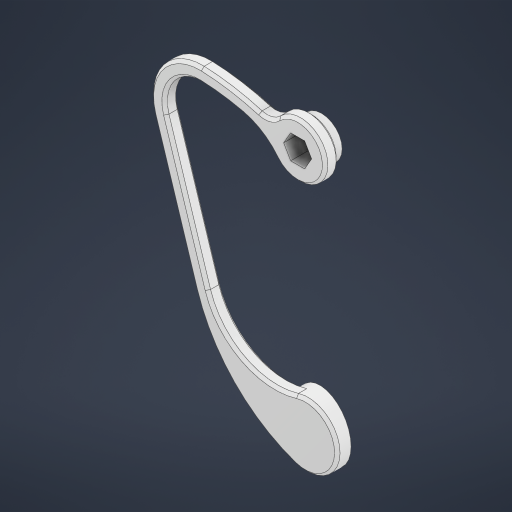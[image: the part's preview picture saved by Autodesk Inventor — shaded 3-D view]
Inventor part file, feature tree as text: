
AUTODESK INVENTOR PART (.ipt)
format: ipt  version: 2023 (Build 270158000, 158)  size: 307,712 bytes
history: native  units: in
note: dims shown in document units (in); Inventor stores cm internally (conversion verified against a paired STEP export)
features: extrude x3, sketch x2, chamfer x1, plane x1
ambient origin geometry x8: Origin, YZ Plane, XZ Plane, XY Plane, X Axis, Y Axis, Z Axis, Center Point
bodies: Solid1 (feature_tree)
feature tree (7):
  sketch  "Sketch1"  dims[d0=0.4724in d2=0.5512in]
  extrude  "Extrusion1"  Depth=0.5512in
  extrude  "Extrusion2"  Depth=0.2992in
  chamfer  "Chamfer1"  Distance=1.939in
  plane  "Work Plane2"
  extrude  "Extrusion4"  Depth=0.1181in TaperAngle=0.0deg
  sketch  "Sketch3"  dims[d12=0.1181in d13=0.2992in d15=1.939in d17=0.1181in d18=0.0in d19=0.7559in d20=0.6019in d21=0.5118in d22=0.1575in d23=0.1201in d26=1.1811in d27=0.3543in d28=0.0866in d29=0.0in d30=0.0236in d31=0.0787in d32=45.0deg d35=0.7874in d36=0.0in]
